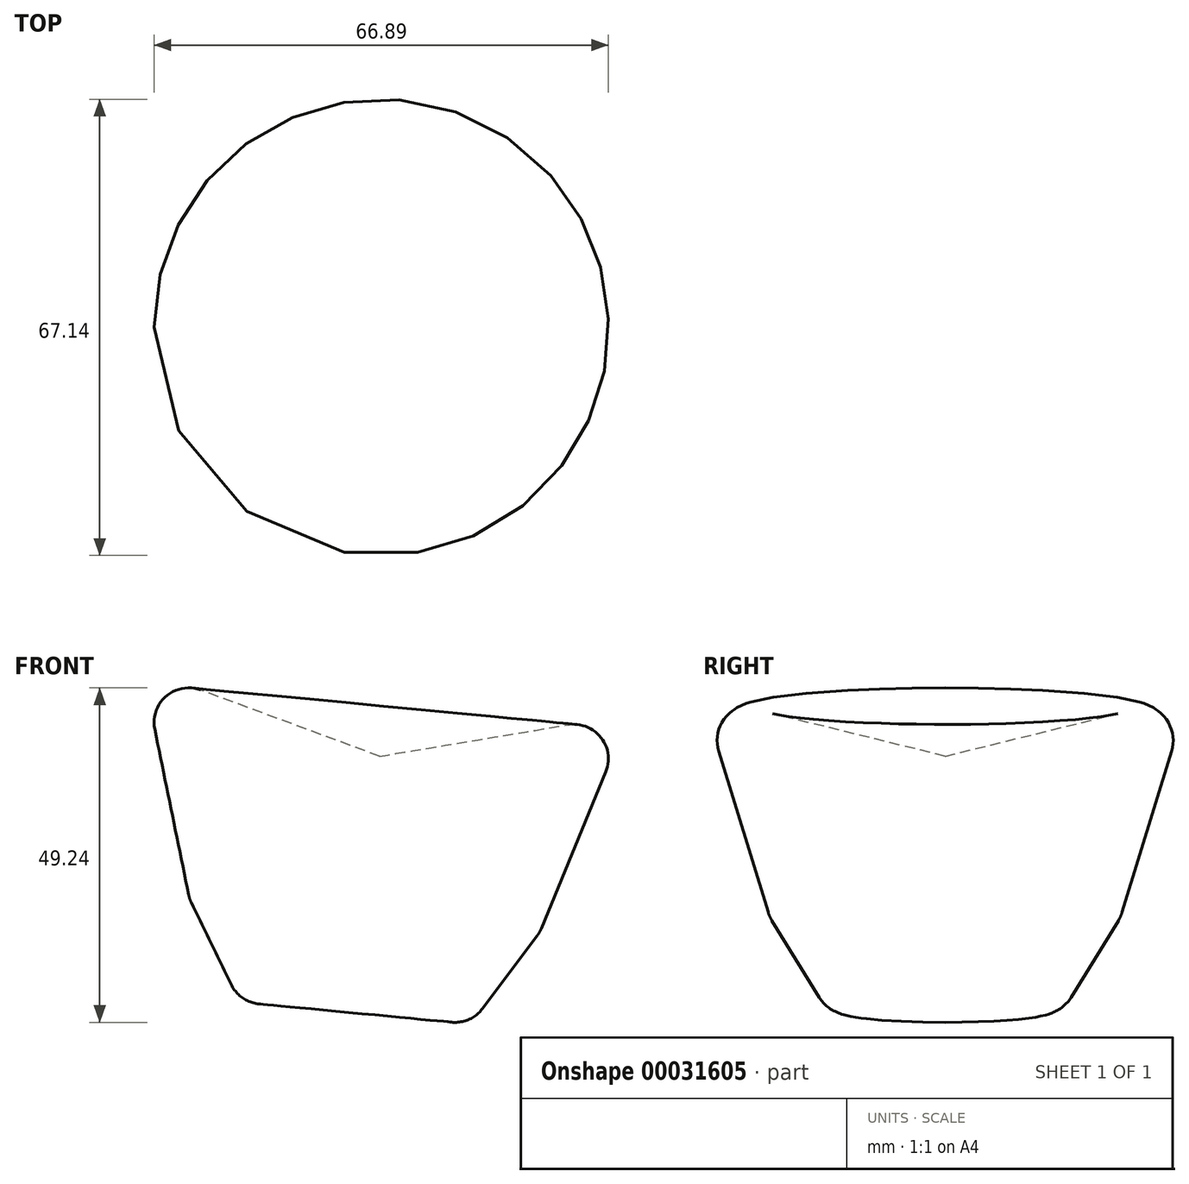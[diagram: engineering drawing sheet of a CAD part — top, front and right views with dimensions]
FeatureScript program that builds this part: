
annotation { "Feature Type Name" : "Feature", "Feature Type Description" : "" }
export const myFeature = defineFeature(function(context is Context, id is Id, definition is map)
    precondition{}
    {
        {
            var Q0;
            Q0=qCreatedBy(makeId("Front.planeOp"),FACE);
            var sketch = newSketch(context, id + "F0", { "sketchPlane" : qUnion([Q0])});
            skLineSegment(sketch, "E0", {"start": v(-13.43, 11.17) * mm, "end": v(-17.01, -26.64) * mm});
            skLineSegment(sketch, "E1", {"start": v(-17.01, -26.64) * mm, "end": v(0, -28.25) * mm});
            skLineSegment(sketch, "E2", {"start": v(0, -28.25) * mm, "end": v(10.11, -14.77) * mm});
            skLineSegment(sketch, "E3", {"start": v(10.11, -14.77) * mm, "end": v(23.34, 17.3) * mm});
            skLineSegment(sketch, "E4", {"start": v(23.34, 17.3) * mm, "end": v(-13.43, 11.17) * mm});
            skSolve(sketch);
        }
        {
            var Q0;
            Q0 = qSketchRegion(id + "F0", true);
            var Q1;
            Q1=sQuery(id+"F0.wireOp",EDGE,"E0");
            revolve(context, id + "F1", {"surfaceOperationType" : NewSurfaceOperationType.NEW, "entities" : qUnion([Q0]), "axis" : qUnion([Q1]), "revolveType" : RevolveType.FULL});
        }
        {
            var Q0;
            Q0=makeQuery(id+"F1.opRevolve","SWEPT_FACE",FACE,{"disambiguationData":[OSD([sQuery(id+"F0.wireOp",EDGE,"E2")])]});
            var Q1;
            Q1=makeQuery(id+"F1.opRevolve","SWEPT_FACE",FACE,{"disambiguationData":[OSD([sQuery(id+"F0.wireOp",EDGE,"E3")])]});
            fillet(context, id + "F2", {"entities" : qUnion([Q0, Q1]), "tangentPropagation" : true, "radius" : 5.08 * mm, "defaultsChanged" : false, "vertexSettings" : [], "allowEdgeOverflow" : false});
        }
    });
